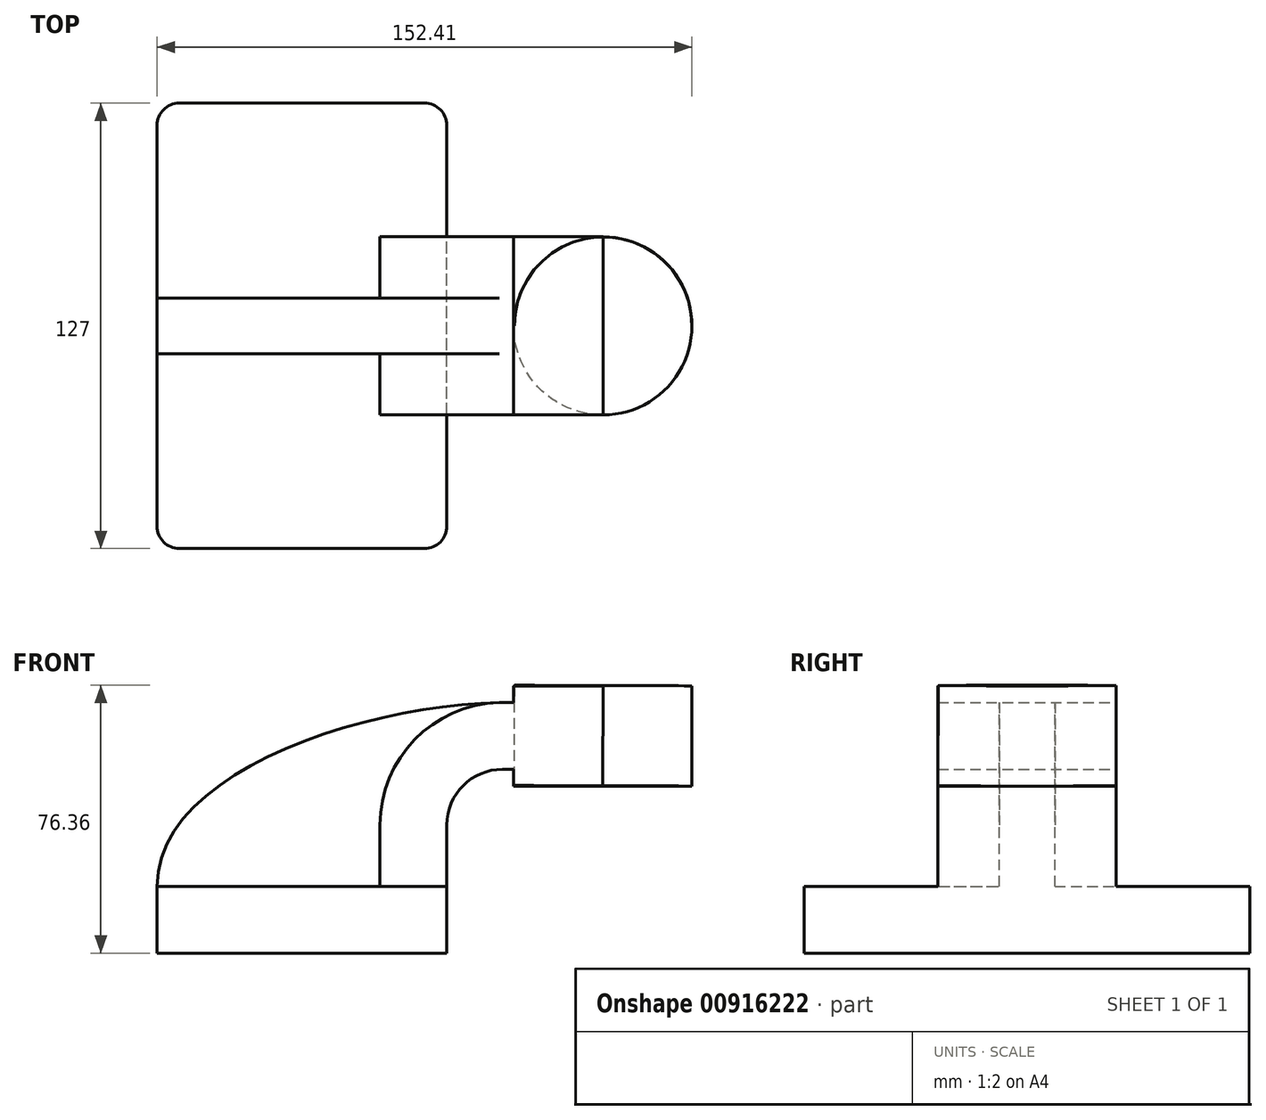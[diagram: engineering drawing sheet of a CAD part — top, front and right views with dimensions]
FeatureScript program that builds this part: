
annotation { "Feature Type Name" : "Feature", "Feature Type Description" : "" }
export const myFeature = defineFeature(function(context is Context, id is Id, definition is map)
    precondition{}
    {
        {
            var Q0;
            Q0=qCreatedBy(makeId("Front.planeOp"),FACE);
            var sketch = newSketch(context, id + "F0", { "sketchPlane" : qUnion([Q0])});
            skLineSegment(sketch, "E0.bottom", {"start": v(-41.28, 9.52) * mm, "end": v(41.28, 9.53) * mm});
            skLineSegment(sketch, "E0.top", {"start": v(-41.28, -9.53) * mm, "end": v(41.28, -9.53) * mm});
            skLineSegment(sketch, "E0.left", {"start": v(-41.28, 9.52) * mm, "end": v(-41.27, -9.53) * mm});
            skLineSegment(sketch, "E0.right", {"start": v(41.28, 9.53) * mm, "end": v(41.28, -9.52) * mm});
            skPoint(sketch, "E0.middle", {"position": v(0, 0) * mm});
            skLineSegment(sketch, "E1.bottom", {"start": v(111.13, 38.1) * mm, "end": v(60.33, 38.1) * mm});
            skLineSegment(sketch, "E1.top", {"start": v(111.13, 66.68) * mm, "end": v(60.32, 66.68) * mm});
            skLineSegment(sketch, "E1.left", {"start": v(111.13, 38.1) * mm, "end": v(111.13, 66.68) * mm});
            skLineSegment(sketch, "E1.right", {"start": v(60.33, 38.1) * mm, "end": v(60.32, 66.68) * mm});
            skPoint(sketch, "E1.middle", {"position": v(85.73, 52.39) * mm});
            skLineSegment(sketch, "E2", {"start": v(41.27, 9.53) * mm, "end": v(41.27, 27) * mm});
            skArc(sketch, "E3", {"start": v(41.27, 27) * mm, "mid": v(45.92, 38.23) * mm, "end": v(57.15, 42.88) * mm});
            skLineSegment(sketch, "E4", {"start": v(57.15, 42.88) * mm, "end": v(85.81, 42.88) * mm});
            skLineSegment(sketch, "E5.0", {"start": v(57.15, 61.93) * mm, "end": v(85.81, 61.93) * mm});
            skArc(sketch, "E5.1", {"start": v(22.22, 27) * mm, "mid": v(32.45, 51.7) * mm, "end": v(57.15, 61.93) * mm});
            skLineSegment(sketch, "E5.2", {"start": v(22.22, 9.53) * mm, "end": v(22.22, 27) * mm});
            skFitSpline(sketch, "E6", {"points": [v(-41.28, 9.52) * mm, v(57.15, 61.93) * mm], "startDerivative": vector(-0.83, 97.8) * mm, "endDerivative": vector(117.05, 1.15) * mm});
            skLineSegment(sketch, "E7", {"start": v(85.73, 38.1) * mm, "end": v(85.81, 66.68) * mm});
            skSolve(sketch);
        }
        {
            var Q0;
            Q0=makeQuery(id+"F0.imprint","IMPRINT",FACE,{"disambiguationData":[TD([[makeQuery(id+"F0.imprint","IMPRINT",EDGE,{"derivedFrom":sQuery(id+"F0.wireOp",EDGE,"E0.top")}),1.0]])]});
            extrude(context, id + "F1", {"entities" : qUnion([Q0]), "endBound" : BoundingType.SYMMETRIC, "depth" : 127 * mm, "offsetDistance" : 25.4 * mm});
        }
        {
            var Q0;
            {var subQ1=sQuery(id+"F0.wireOp",EDGE,"E1.bottom");Q0=makeQuery(id+"F0.imprint","IMPRINT",FACE,{"disambiguationData":[TD([[makeQuery(id+"F0.imprint","IMPRINT",EDGE,{"derivedFrom":subQ1}),-1.0]])]});}
            var Q1;
            {var subQ1=sQuery(id+"F0.wireOp",EDGE,"E2");Q1=makeQuery(id+"F0.imprint","IMPRINT",FACE,{"disambiguationData":[TD([[makeQuery(id+"F0.imprint","IMPRINT",EDGE,{"derivedFrom":subQ1}),1.0]])]});}
            var Q2;
            {var subQ0=sQuery(id+"F0.wireOp",EDGE,"E4");var subQ1=sQuery(id+"F0.wireOp",EDGE,"E1.right");var subQ2=makeQuery(id+"F0.imprint","INTERSECT",VERTEX,{"derivedFrom":[subQ1,subQ0]});Q2=makeQuery(id+"F0.imprint","IMPRINT",FACE,{"disambiguationData":[TD([[makeQuery(id+"F0.imprint","IMPRINT",EDGE,{"disambiguationData":[TD([[subQ2,-1.0]])],"derivedFrom":subQ1}),-1.0]])]});}
            var Q3;
            {var subQ0=sQuery(id+"F0.wireOp",EDGE,"E1.right");var subQ1=sQuery(id+"F0.wireOp",EDGE,"E1.top");var subQ2=makeQuery(id+"F0.imprint","INTERSECT",VERTEX,{"derivedFrom":[subQ1,subQ0]});Q3=makeQuery(id+"F0.imprint","IMPRINT",FACE,{"disambiguationData":[TD([[makeQuery(id+"F0.imprint","IMPRINT",EDGE,{"disambiguationData":[TD([[subQ2,1.0]])],"derivedFrom":subQ1}),1.0]])]});}
            extrude(context, id + "F2", {"entities" : qUnion([Q0, Q1, Q2, Q3]), "operationType" : NewBodyOperationType.ADD, "endBound" : BoundingType.SYMMETRIC, "depth" : 50.8 * mm, "offsetDistance" : 25.4 * mm});
        }
        {
            var Q0;
            {var subQ3=sQuery(id+"F0.wireOp",EDGE,"E5.2");Q0=makeQuery(id+"F0.imprint","IMPRINT",FACE,{"disambiguationData":[TD([[makeQuery(id+"F0.imprint","IMPRINT",EDGE,{"derivedFrom":subQ3}),1.0]])]});}
            extrude(context, id + "F3", {"entities" : qUnion([Q0]), "operationType" : NewBodyOperationType.ADD, "endBound" : BoundingType.SYMMETRIC, "depth" : 15.88 * mm, "offsetDistance" : 25.4 * mm});
        }
        {
            var Q0;
            {var subQ4=sQuery(id+"F0.wireOp",EDGE,"E1.left");Q0=makeQuery(id+"F0.imprint","IMPRINT",FACE,{"disambiguationData":[TD([[makeQuery(id+"F0.imprint","IMPRINT",EDGE,{"derivedFrom":subQ4}),1.0]])]});}
            var Q1;
            Q1=sQuery(id+"F0.wireOp",EDGE,"E7");
            revolve(context, id + "F4", {"surfaceOperationType" : NewSurfaceOperationType.NEW, "entities" : qUnion([Q0]), "axis" : qUnion([Q1]), "revolveType" : RevolveType.FULL});
        }
        {
            var Q0;
            Q0=makeQuery(id+"F1.opExtrude","CAP_EDGE",EDGE,{"disambiguationData":[OSD([sQuery(id+"F0.wireOp",EDGE,"E0.right")])],"isStart":false});
            var Q1;
            Q1=makeQuery(id+"F1.opExtrude","CAP_EDGE",EDGE,{"disambiguationData":[OSD([sQuery(id+"F0.wireOp",EDGE,"E0.right")])],"isStart":true});
            fillet(context, id + "F5", {"entities" : qUnion([Q0, Q1]), "radius" : 6.35 * mm, "tangentPropagation" : true, "allowEdgeOverflow" : false});
        }
        {
            var Q0;
            Q0=makeQuery(id+"F1.opExtrude","CAP_EDGE",EDGE,{"disambiguationData":[OSD([sQuery(id+"F0.wireOp",EDGE,"E0.left")])],"isStart":false});
            var Q1;
            Q1=makeQuery(id+"F1.opExtrude","CAP_EDGE",EDGE,{"disambiguationData":[OSD([sQuery(id+"F0.wireOp",EDGE,"E0.left")])],"isStart":true});
            fillet(context, id + "F6", {"entities" : qUnion([Q0, Q1]), "radius" : 6.35 * mm, "tangentPropagation" : true, "allowEdgeOverflow" : false});
        }
    });
